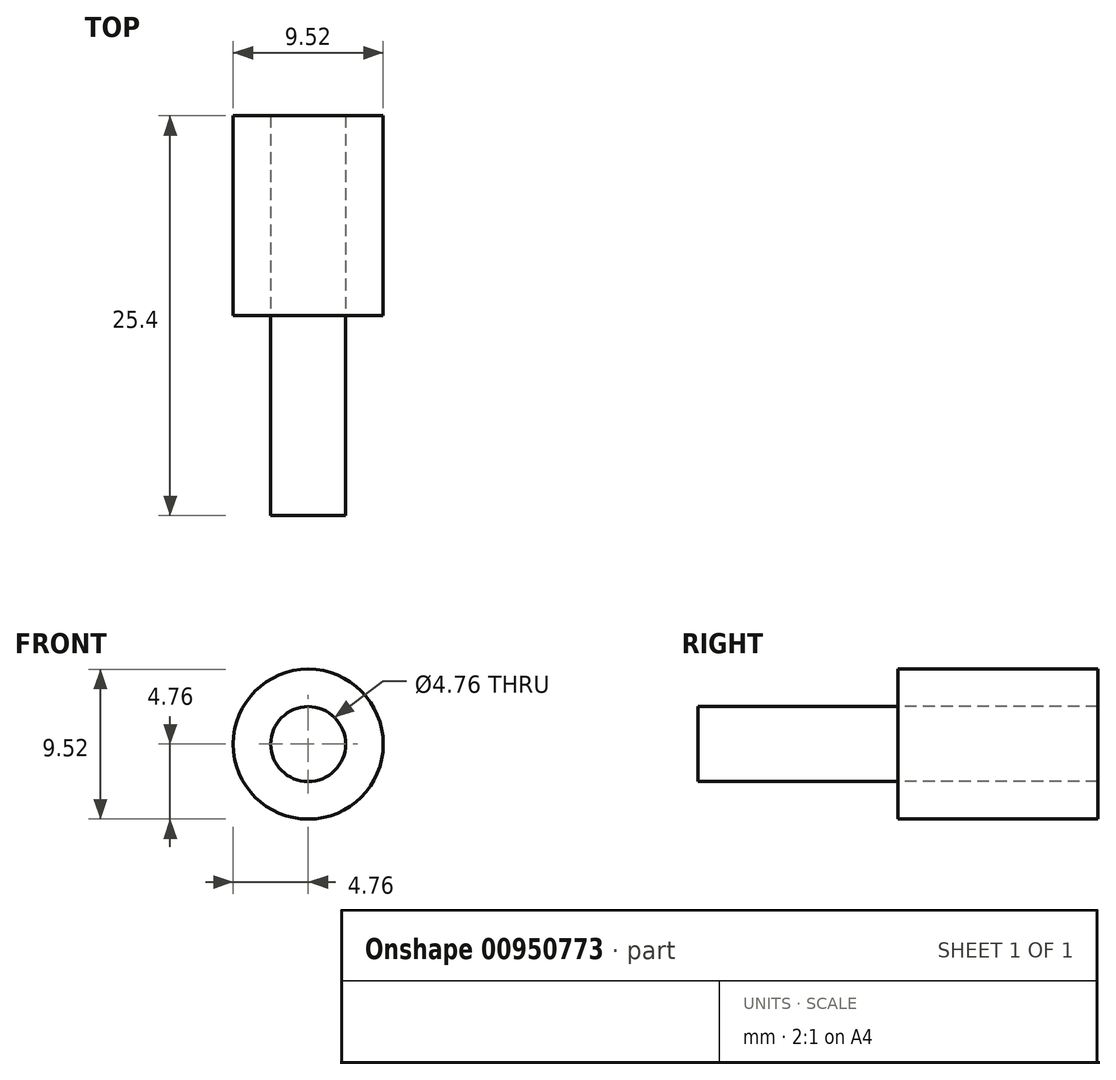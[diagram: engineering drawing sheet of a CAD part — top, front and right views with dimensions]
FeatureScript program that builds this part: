
annotation { "Feature Type Name" : "Feature", "Feature Type Description" : "" }
export const myFeature = defineFeature(function(context is Context, id is Id, definition is map)
    precondition{}
    {
        {
            var Q0;
            Q0=qCreatedBy(makeId("Front.planeOp"),FACE);
            var sketch = newSketch(context, id + "F0", { "sketchPlane" : qUnion([Q0])});
            skLineSegment(sketch, "E0", {"start": v(0, 0) * mm, "end": v(-4.76, 0) * mm});
            skCircle(sketch, "E1", {"center": v(0, 0) * mm, "radius": 4.76 * mm});
            skLineSegment(sketch, "E2", {"start": v(0, 0) * mm, "end": v(0, -2.38) * mm});
            skCircle(sketch, "E3", {"center": v(0, 0) * mm, "radius": 2.38 * mm});
            skSolve(sketch);
        }
        {
            var Q0;
            Q0=makeQuery(id+"F0.imprint","IMPRINT",FACE,{"disambiguationData":[TD([[makeQuery(id+"F0.imprint","IMPRINT",EDGE,{"derivedFrom":sQuery(id+"F0.wireOp",EDGE,"E1")}),1.0]])]});
            extrude(context, id + "F1", {"entities" : qUnion([Q0]), "oppositeDirection" : true, "depth" : 12.7 * mm, "offsetDistance" : 25.4 * mm});
        }
        {
            var Q0;
            {var subQ0=sQuery(id+"F0.wireOp",EDGE,"E2");Q0=makeQuery(id+"F0.imprint","IMPRINT",FACE,{"disambiguationData":[TD([[makeQuery(id+"F0.imprint","IMPRINT",EDGE,{"derivedFrom":subQ0}),1.0]])]});}
            var Q1;
            {var subQ0=sQuery(id+"F0.wireOp",EDGE,"E2");Q1=makeQuery(id+"F0.imprint","IMPRINT",FACE,{"disambiguationData":[TD([[makeQuery(id+"F0.imprint","IMPRINT",EDGE,{"derivedFrom":subQ0}),-1.0]])]});}
            extrude(context, id + "F2", {"entities" : qUnion([Q0, Q1]), "depth" : 12.7 * mm, "offsetDistance" : 25.4 * mm});
        }
    });
